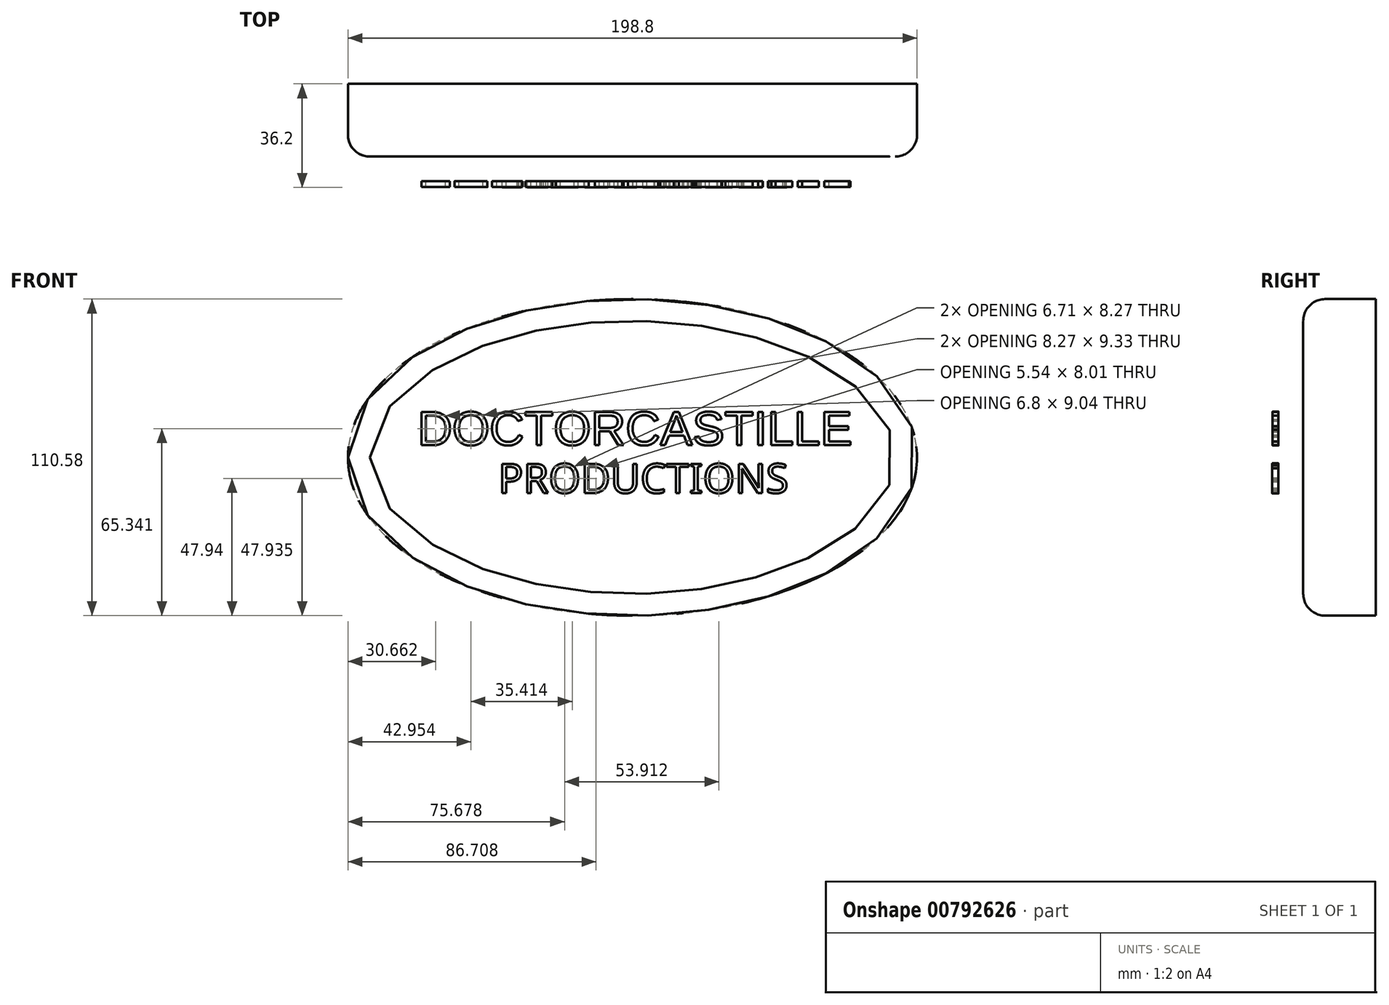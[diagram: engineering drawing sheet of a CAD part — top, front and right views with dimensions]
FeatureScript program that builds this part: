
annotation { "Feature Type Name" : "Feature", "Feature Type Description" : "" }
export const myFeature = defineFeature(function(context is Context, id is Id, definition is map)
    precondition{}
    {
        {
            var Q0;
            Q0=qCreatedBy(makeId("Front.planeOp"),FACE);
            var sketch = newSketch(context, id + "F0", { "sketchPlane" : qUnion([Q0])});
            skEllipse(sketch, "E0", {"center": v(0, 0) * mm, "majorRadius": 99.4 * mm, "minorRadius": 55.3 * mm, "majorAxis": v(-1, 0)});
            skSolve(sketch);
        }
        {
            var Q0;
            Q0 = qSketchRegion(id + "F0", true);
            extrude(context, id + "F1", {"entities" : qUnion([Q0]), "depth" : 25.4 * mm, "offsetDistance" : 25.4 * mm});
        }
        {
            var Q0;
            Q0=makeQuery(id+"F1.opExtrude","CAP_EDGE",EDGE,{"disambiguationData":[OSD([sQuery(id+"F0.wireOp",EDGE,"E0")])],"isStart":false});
            fillet(context, id + "F2", {"entities" : qUnion([Q0]), "radius" : 7.62 * mm, "tangentPropagation" : true, "allowEdgeOverflow" : false});
        }
        {
            var Q0;
            Q0=qCreatedBy(makeId("Front.planeOp"),FACE);
            cPlane(context, id + "F3", {"entities" : qUnion([Q0]), "cplaneType" : CPlaneType.OFFSET, "offset" : 34.04 * mm, "width" : 152.4 * mm, "height" : 152.4 * mm});
        }
        {
            var Q0;
            Q0=qCreatedBy(id+"F3.planeOp",FACE);
            var sketch = newSketch(context, id + "F4", { "sketchPlane" : qUnion([Q0])});
            skText(sketch, "E1", { "text": "DOCTORCASTILLE", "fontName": "Arimo-Regular.ttf"});
            const initialGuessF4  = {"E1": [-0.07508, 0.00428, 1, 0, 0.01208]};
            skSetInitialGuess(sketch, initialGuessF4);
            skSolve(sketch);
        }
        {
            var Q0;
            Q0 = qSketchRegion(id + "F4", true);
            extrude(context, id + "F5", {"entities" : qUnion([Q0]), "depth" : 2.03 * mm, "offsetDistance" : 25.4 * mm});
        }
        {
            var Q0;
            Q0=qCreatedBy(id+"F3.planeOp",FACE);
            var sketch = newSketch(context, id + "F6", { "sketchPlane" : qUnion([Q0])});
            skText(sketch, "E2", { "text": "PRODUCTIONS", "fontName": "NotoSans-Regular.ttf"});
            const initialGuessF6  = {"E2": [-0.04686, -0.01246, 1, 0, 0.0103]};
            skSetInitialGuess(sketch, initialGuessF6);
            skSolve(sketch);
        }
        {
            var Q0;
            Q0 = qSketchRegion(id + "F6", true);
            extrude(context, id + "F7", {"entities" : qUnion([Q0]), "depth" : 2.16 * mm, "offsetDistance" : 25.4 * mm});
        }
    });
